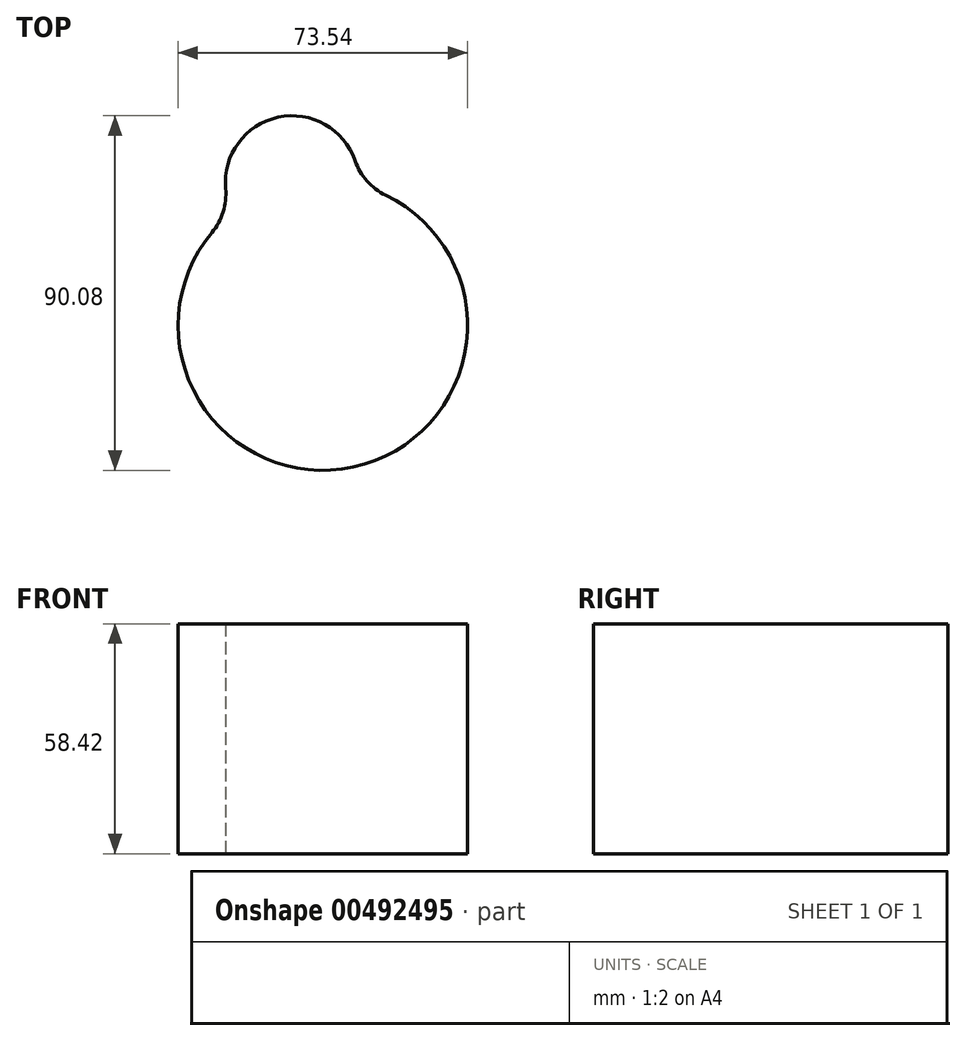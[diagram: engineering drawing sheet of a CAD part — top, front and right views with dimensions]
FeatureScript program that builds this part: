
annotation { "Feature Type Name" : "Feature", "Feature Type Description" : "" }
export const myFeature = defineFeature(function(context is Context, id is Id, definition is map)
    precondition{}
    {
        {
            var Q0;
            Q0=qCreatedBy(makeId("Top.planeOp"),FACE);
            var sketch = newSketch(context, id + "F0", { "sketchPlane" : qUnion([Q0])});
            skCircle(sketch, "E0", {"center": v(0, 0) * mm, "radius": 36.77 * mm});
            skArc(sketch, "E1", {"start": v(9.1, 35.63) * mm, "mid": v(-11.38, 52.93) * mm, "end": v(-22.95, 28.73) * mm});
            skSolve(sketch);
        }
        {
            var Q0;
            {var subQ0=sQuery(id+"F0.wireOp",EDGE,"E1");var subQ1=sQuery(id+"F0.wireOp",EDGE,"E0");var subQ2=makeQuery(id+"F0.imprint","INTERSECT",VERTEX,{"disambiguationData":[OD(0.0)],"derivedFrom":[subQ1,subQ0]});Q0=makeQuery(id+"F0.imprint","IMPRINT",FACE,{"disambiguationData":[TD([[makeQuery(id+"F0.imprint","IMPRINT",EDGE,{"disambiguationData":[TD([[subQ2,-1.0]])],"derivedFrom":subQ1}),1.0]])]});}
            var Q1;
            {var subQ0=sQuery(id+"F0.wireOp",EDGE,"E1");Q1=makeQuery(id+"F0.imprint","IMPRINT",FACE,{"disambiguationData":[TD([[makeQuery(id+"F0.imprint","IMPRINT",EDGE,{"derivedFrom":subQ0}),1.0]])]});}
            extrude(context, id + "F1", {"entities" : qUnion([Q0, Q1]), "depth" : 58.42 * mm});
        }
        {
            var Q0;
            {var subQ0=sQuery(id+"F0.wireOp",EDGE,"E1");var subQ1=sQuery(id+"F0.wireOp",EDGE,"E0");Q0=makeQuery(id+"F1.opExtrude","SWEPT_EDGE",EDGE,{"disambiguationData":[OSD([subQ1,subQ0]),TDD([makeQuery(id+"F0.imprint","INTERSECT",VERTEX,{"disambiguationData":[OD(1.0)],"derivedFrom":[subQ1,subQ0]})])]});}
            var Q1;
            {var subQ0=sQuery(id+"F0.wireOp",EDGE,"E1");var subQ1=sQuery(id+"F0.wireOp",EDGE,"E0");Q1=makeQuery(id+"F1.opExtrude","SWEPT_EDGE",EDGE,{"disambiguationData":[OSD([subQ1,subQ0]),TDD([makeQuery(id+"F0.imprint","INTERSECT",VERTEX,{"disambiguationData":[OD(0.0)],"derivedFrom":[subQ1,subQ0]})])]});}
            fillet(context, id + "F2", {"entities" : qUnion([Q0, Q1]), "radius" : 15.24 * mm, "tangentPropagation" : true, "allowEdgeOverflow" : false});
        }
        {
            var Q0;
            Q0=makeQuery(id+"F1.opExtrude","CAP_FACE",FACE,{"disambiguationData":[OSD([sQuery(id+"F0.wireOp",EDGE,"E0"),sQuery(id+"F0.wireOp",EDGE,"E1")])],"isStart":false});
            var sketch = newSketch(context, id + "F3", { "sketchPlane" : qUnion([Q0])});
            skCircle(sketch, "E2", {"center": v(-1.75, 3.43) * mm, "radius": 6.83 * mm});
            skSolve(sketch);
        }
        {
            var Q0;
            Q0=makeQuery(id+"F3.imprint","IMPRINT",FACE,{"disambiguationData":[TD([[makeQuery(id+"F3.imprint","IMPRINT",EDGE,{"derivedFrom":sQuery(id+"F3.wireOp",EDGE,"E2")}),1.0]])]});
            extrude(context, id + "F4", {"entities" : qUnion([Q0]), "operationType" : NewBodyOperationType.ADD, "depth" : -30.48 * mm});
        }
    });
